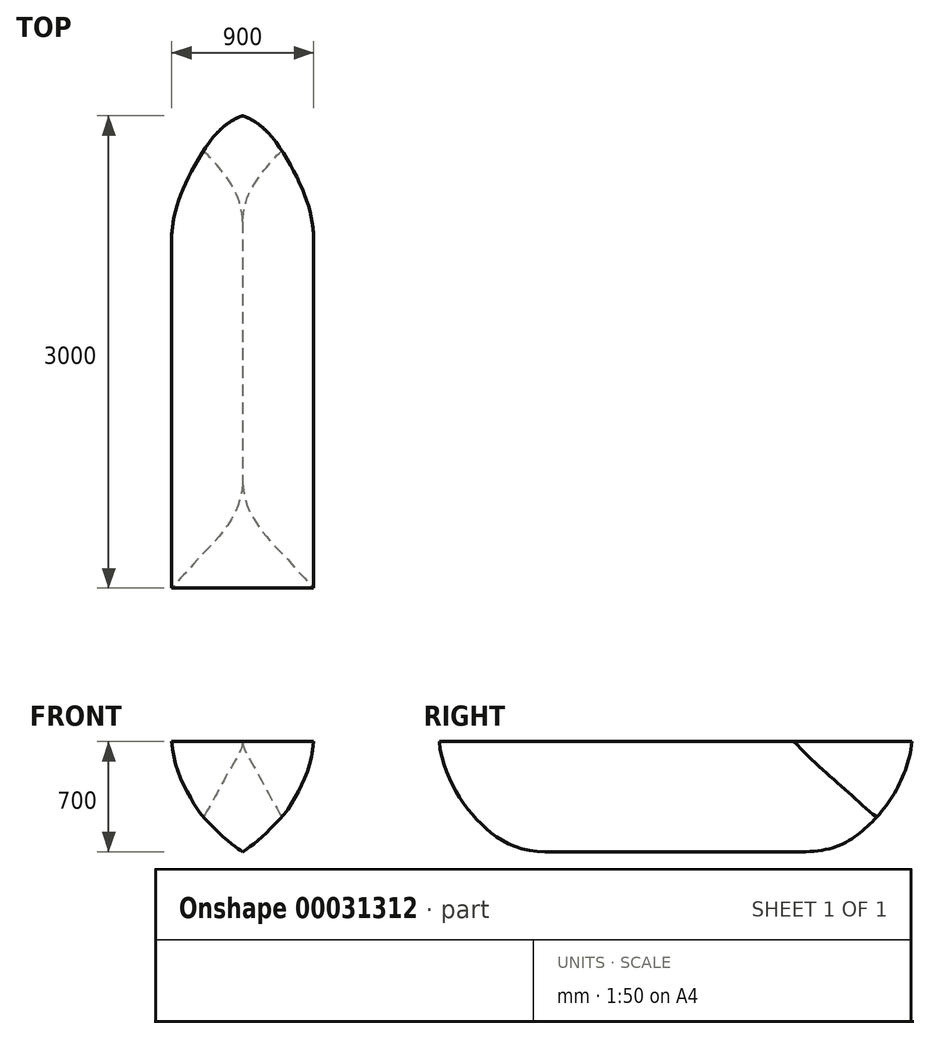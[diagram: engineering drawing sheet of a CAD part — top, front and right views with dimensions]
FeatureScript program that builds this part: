
annotation { "Feature Type Name" : "Feature", "Feature Type Description" : "" }
export const myFeature = defineFeature(function(context is Context, id is Id, definition is map)
    precondition{}
    {
        {
            var Q0;
            Q0=qCreatedBy(makeId("Top.planeOp"),FACE);
            var sketch = newSketch(context, id + "F0", { "sketchPlane" : qUnion([Q0])});
            skLineSegment(sketch, "E0.rect.bottom", {"start": v(450, 1500) * mm, "end": v(-450, 1500) * mm});
            skLineSegment(sketch, "E0.rect.top", {"start": v(450, -1500) * mm, "end": v(-450, -1500) * mm});
            skLineSegment(sketch, "E0.rect.left", {"start": v(450, 1500) * mm, "end": v(450, -1500) * mm});
            skLineSegment(sketch, "E0.rect.right", {"start": v(-450, 1500) * mm, "end": v(-450, -1500) * mm});
            skPoint(sketch, "E0.rect.middle", {"position": v(0, 0) * mm});
            skFitSpline(sketch, "E1", {"points": [v(0, -1500) * mm, v(225.1, -1312.13) * mm, v(392.82, -999.77) * mm, v(450, -749.75) * mm], "startDerivative": vector(918.35, 329.31) * mm, "endDerivative": vector(87.59, 936.13) * mm});
            skFitSpline(sketch, "E2.MirrorCS", {"points": [v(0, -1500) * mm, v(-225.1, -1312.13) * mm, v(-392.82, -999.77) * mm, v(-450, -749.75) * mm], "startDerivative": vector(-918.35, 329.31) * mm, "endDerivative": vector(-87.59, 936.13) * mm});
            skFitSpline(sketch, "E3.MirrorCS", {"points": [v(0, -1500) * mm, v(225.1, -1312.13) * mm, v(392.82, -999.77) * mm, v(450, -749.75) * mm], "startDerivative": vector(918.35, 329.31) * mm, "endDerivative": vector(87.59, 936.13) * mm});
            skFitSpline(sketch, "E4.MirrorCS", {"points": [v(0, -1500) * mm, v(-225.1, -1312.13) * mm, v(-392.82, -999.77) * mm, v(-450, -749.75) * mm], "startDerivative": vector(-918.35, 329.31) * mm, "endDerivative": vector(-87.59, 936.13) * mm});
            skFitSpline(sketch, "E5.MirrorCS", {"points": [v(0, -1500) * mm, v(225.1, -1312.13) * mm, v(392.82, -999.77) * mm, v(450, -749.75) * mm], "startDerivative": vector(918.35, 329.31) * mm, "endDerivative": vector(87.59, 936.13) * mm});
            skFitSpline(sketch, "E6.MirrorCS", {"points": [v(0, 1500) * mm, v(-225.1, 1312.13) * mm, v(-392.82, 999.77) * mm, v(-450, 749.75) * mm], "startDerivative": vector(-918.35, -329.31) * mm, "endDerivative": vector(-87.59, -936.13) * mm});
            skFitSpline(sketch, "E7.MirrorCS", {"points": [v(0, 1500) * mm, v(225.1, 1312.13) * mm, v(392.82, 999.77) * mm, v(450, 749.75) * mm], "startDerivative": vector(918.35, -329.31) * mm, "endDerivative": vector(87.59, -936.13) * mm});
            skLineSegment(sketch, "E8", {"start": v(-450, 749.75) * mm, "end": v(-450, -749.75) * mm});
            skLineSegment(sketch, "E9", {"start": v(450, -749.75) * mm, "end": v(450, 749.75) * mm});
            skSolve(sketch);
        }
        {
            var Q0;
            Q0 = qSketchRegion(id + "F0", true);
            extrude(context, id + "F1", {"entities" : qUnion([Q0]), "depth" : 700 * mm});
        }
        {
            var Q0;
            Q0=makeQuery(id+"F1.opExtrude","SWEPT_FACE",FACE,{"disambiguationData":[OSD([sQuery(id+"F0.wireOp",EDGE,"E0.rect.right"),sQuery(id+"F0.wireOp",EDGE,"E8")])]});
            var sketch = newSketch(context, id + "F2", { "sketchPlane" : qUnion([Q0])});
            skPoint(sketch, "E10.0", {"position": v(-749.75, 0) * mm});
            skFitSpline(sketch, "E11", {"points": [v(-749.75, 0) * mm, v(-999.77, 26.24) * mm, v(-1312.13, 261.36) * mm, v(-1437.1, 465.65) * mm, v(-1500, 700) * mm], "startDerivative": vector(-266.28, 0) * mm, "endDerivative": vector(0, 891.28) * mm});
            skPoint(sketch, "E12.0", {"position": v(-999.77, 0) * mm});
            skPoint(sketch, "E13.0", {"position": v(-1312.13, 0) * mm});
            skPoint(sketch, "E14.1", {"position": v(0, 0) * mm});
            skLineSegment(sketch, "E15", {"start": v(0, 0) * mm, "end": v(0, 700) * mm});
            skFitSpline(sketch, "E16.MirrorCS", {"points": [v(749.75, 0) * mm, v(999.77, 26.24) * mm, v(1312.13, 261.36) * mm, v(1437.1, 465.65) * mm, v(1500, 700) * mm], "startDerivative": vector(266.28, 0) * mm, "endDerivative": vector(0, 891.28) * mm});
            skSolve(sketch);
        }
        {
            var Q0;
            Q0=makeQuery(id+"F1.opExtrude","SWEPT_FACE",FACE,{"disambiguationData":[OSD([sQuery(id+"F0.wireOp",EDGE,"E0.rect.top")])]});
            var sketch = newSketch(context, id + "F3", { "sketchPlane" : qUnion([Q0])});
            skPoint(sketch, "E17.0", {"position": v(0, 0) * mm});
            skPoint(sketch, "E18.0", {"position": v(-450, 0) * mm});
            skPoint(sketch, "E19.0", {"position": v(-450, 261.36) * mm});
            skPoint(sketch, "E20.0", {"position": v(-450, 465.65) * mm});
            skFitSpline(sketch, "E21", {"points": [v(-450, 700) * mm, v(-393.75, 465.65) * mm, v(-281.25, 261.36) * mm, v(-225, 196.02) * mm, v(0, 0) * mm], "startDerivative": vector(116.06, -1184.79) * mm, "endDerivative": vector(1084.41, -702) * mm});
            skPoint(sketch, "E22", {"position": v(-225, 0) * mm});
            skPoint(sketch, "E23", {"position": v(-337.5, 0) * mm});
            skPoint(sketch, "E24", {"position": v(-112.5, 0) * mm});
            skPoint(sketch, "E25", {"position": v(-168.75, 0) * mm});
            skPoint(sketch, "E26", {"position": v(-281.25, 0) * mm});
            skPoint(sketch, "E27", {"position": v(-393.75, 0) * mm});
            skPoint(sketch, "E28", {"position": v(-450, 130.68) * mm});
            skPoint(sketch, "E29", {"position": v(-450, 196.02) * mm});
            skLineSegment(sketch, "E30", {"start": v(0, 0) * mm, "end": v(0, 700) * mm});
            skFitSpline(sketch, "E31.MirrorCS", {"points": [v(450, 700) * mm, v(393.75, 465.65) * mm, v(281.25, 261.36) * mm, v(225, 196.02) * mm, v(0, 0) * mm], "startDerivative": vector(-116.06, -1184.79) * mm, "endDerivative": vector(-1084.41, -702) * mm});
            skSolve(sketch);
        }
        {
            var Q0;
            {var subQ2=sQuery(id+"F3.wireOp",EDGE,"E21");Q0=makeQuery(id+"F3.imprint","IMPRINT",FACE,{"disambiguationData":[TD([[makeQuery(id+"F3.imprint","IMPRINT",EDGE,{"derivedFrom":subQ2}),-1.0]])]});}
            var Q1;
            {var subQ2=sQuery(id+"F3.wireOp",EDGE,"E31.MirrorCS");Q1=makeQuery(id+"F3.imprint","IMPRINT",FACE,{"disambiguationData":[TD([[makeQuery(id+"F3.imprint","IMPRINT",EDGE,{"derivedFrom":subQ2}),1.0]])]});}
            extrude(context, id + "F4", {"entities" : qUnion([Q0, Q1]), "operationType" : NewBodyOperationType.REMOVE, "oppositeDirection" : true, "depth" : 3000 * mm});
        }
        {
            var Q0;
            {var subQ0=sQuery(id+"F0.wireOp",EDGE,"E4.MirrorCS");Q0=makeQuery(id+"F0.imprint","IMPRINT",FACE,{"disambiguationData":[TD([[makeQuery(id+"F0.imprint","IMPRINT",EDGE,{"derivedFrom":subQ0}),1.0]])]});}
            var Q1;
            {var subQ0=sQuery(id+"F0.wireOp",EDGE,"E5.MirrorCS");Q1=makeQuery(id+"F0.imprint","IMPRINT",FACE,{"disambiguationData":[TD([[makeQuery(id+"F0.imprint","IMPRINT",EDGE,{"derivedFrom":subQ0}),-1.0]])]});}
            var Q2;
            {var subQ0=sQuery(id+"F0.wireOp",EDGE,"E7.MirrorCS");Q2=makeQuery(id+"F0.imprint","IMPRINT",FACE,{"disambiguationData":[TD([[makeQuery(id+"F0.imprint","IMPRINT",EDGE,{"derivedFrom":subQ0}),1.0]])]});}
            var Q3;
            {var subQ0=sQuery(id+"F0.wireOp",EDGE,"E6.MirrorCS");Q3=makeQuery(id+"F0.imprint","IMPRINT",FACE,{"disambiguationData":[TD([[makeQuery(id+"F0.imprint","IMPRINT",EDGE,{"derivedFrom":subQ0}),-1.0]])]});}
            extrude(context, id + "F5", {"entities" : qUnion([Q0, Q1, Q2, Q3]), "operationType" : NewBodyOperationType.REMOVE, "depth" : 700 * mm});
        }
        {
            var Q0;
            {var subQ0=sQuery(id+"F0.wireOp",EDGE,"E0.rect.right");var subQ5=makeQuery(id+"F1.opExtrude","SWEPT_EDGE",EDGE,{"disambiguationData":[OSD([sQuery(id+"F0.wireOp",EDGE,"E0.rect.bottom"),subQ0])]});Q0=makeQuery(id+"F2.imprint","IMPRINT",FACE,{"disambiguationData":[TD([[makeQuery(id+"F2.imprint","IMPRINT",EDGE,{"derivedFrom":subQ5}),1.0]])]});}
            var Q1;
            {var subQ0=sQuery(id+"F0.wireOp",EDGE,"E0.rect.right");var subQ5=makeQuery(id+"F1.opExtrude","SWEPT_EDGE",EDGE,{"disambiguationData":[OSD([sQuery(id+"F0.wireOp",EDGE,"E0.rect.top"),subQ0])]});Q1=makeQuery(id+"F2.imprint","IMPRINT",FACE,{"disambiguationData":[TD([[makeQuery(id+"F2.imprint","IMPRINT",EDGE,{"derivedFrom":subQ5}),-1.0]])]});}
            extrude(context, id + "F6", {"entities" : qUnion([Q0, Q1]), "operationType" : NewBodyOperationType.REMOVE, "oppositeDirection" : true, "depth" : 900 * mm});
        }
    });
